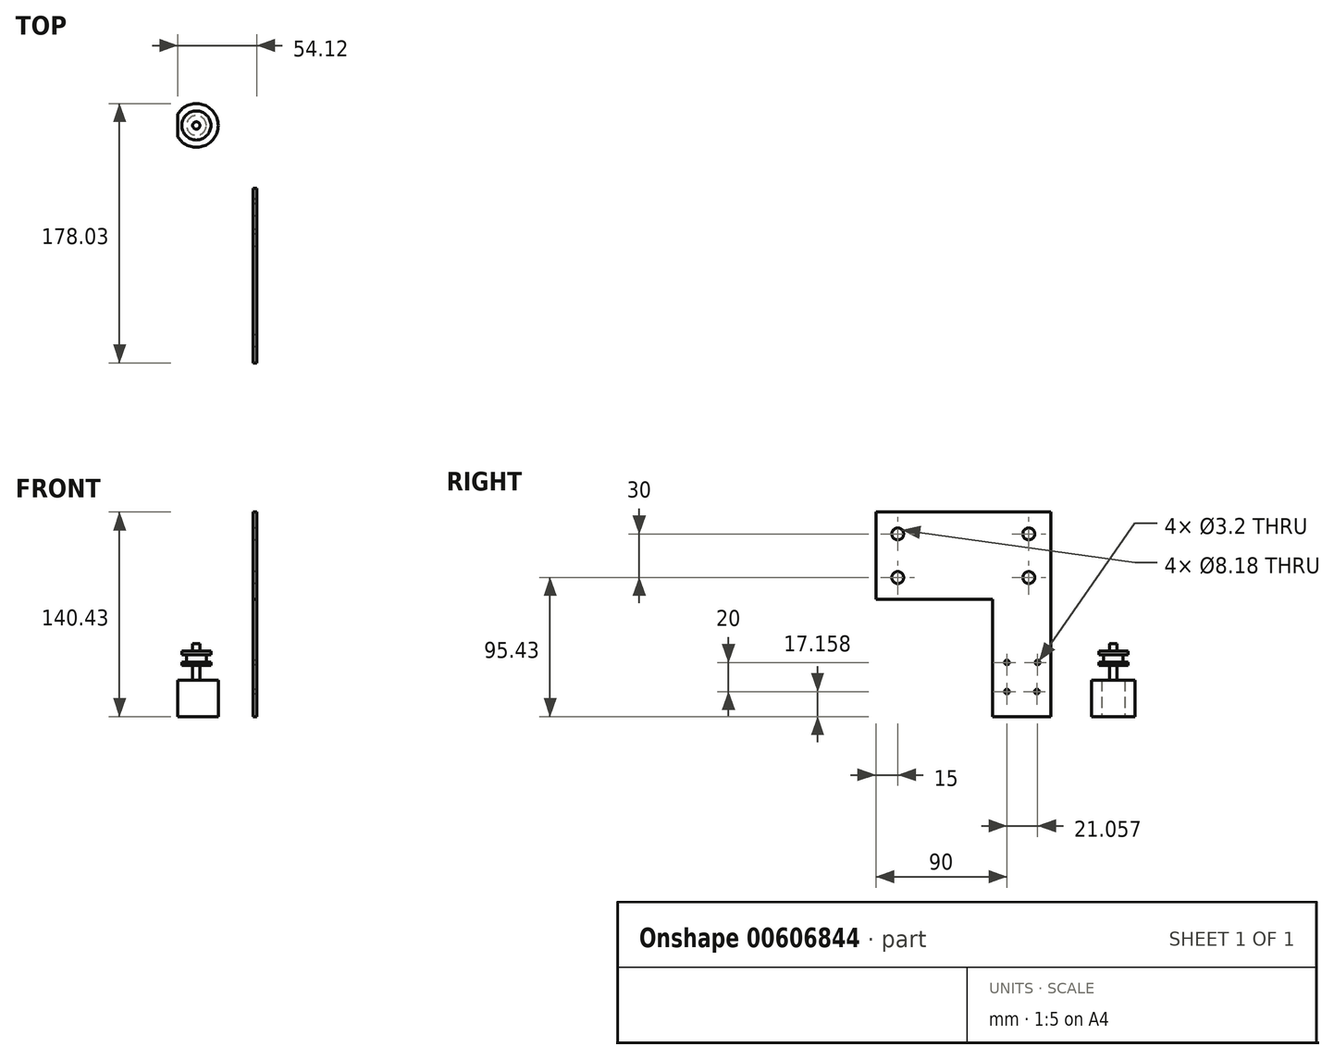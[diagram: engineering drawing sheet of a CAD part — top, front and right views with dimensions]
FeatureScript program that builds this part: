
annotation { "Feature Type Name" : "Feature", "Feature Type Description" : "" }
export const myFeature = defineFeature(function(context is Context, id is Id, definition is map)
    precondition{}
    {
        {
            var Q0;
            Q0=qCreatedBy(makeId("Right.planeOp"),FACE);
            var sketch = newSketch(context, id + "F0", { "sketchPlane" : qUnion([Q0])});
            skLineSegment(sketch, "E0", {"start": v(0, 0) * mm, "end": v(0, 140.43) * mm});
            skLineSegment(sketch, "E1", {"start": v(0, 140.43) * mm, "end": v(-120, 140.43) * mm});
            skLineSegment(sketch, "E2", {"start": v(-120, 140.43) * mm, "end": v(-120, 80.43) * mm});
            skLineSegment(sketch, "E3", {"start": v(-120, 80.43) * mm, "end": v(-40, 80.43) * mm});
            skLineSegment(sketch, "E4", {"start": v(-40, 80.43) * mm, "end": v(-40, 0) * mm});
            skLineSegment(sketch, "E5", {"start": v(-40, 0) * mm, "end": v(0, 0) * mm});
            skLineSegment(sketch, "E6", {"start": v(-40, 60) * mm, "end": v(0, 60) * mm, "construction": true});
            skLineSegment(sketch, "E7", {"start": v(-40, 30) * mm, "end": v(0, 30) * mm, "construction": true});
            skCircle(sketch, "E8.MirrorC", {"center": v(-9.46, 17.16) * mm, "radius": 1.6 * mm});
            skCircle(sketch, "E9", {"center": v(-8.94, 37.16) * mm, "radius": 1.6 * mm});
            skCircle(sketch, "E10.MirrorC", {"center": v(-30, 37.16) * mm, "radius": 1.6 * mm});
            skCircle(sketch, "E11.MirrorC", {"center": v(-30, 17.16) * mm, "radius": 1.6 * mm});
            skPoint(sketch, "E12.endSnap0", {"position": v(-60, 110.43) * mm});
            skCircle(sketch, "E13", {"center": v(-15, 125.43) * mm, "radius": 4.1 * mm});
            skCircle(sketch, "E14.MirrorC", {"center": v(-105, 125.43) * mm, "radius": 4.1 * mm});
            skCircle(sketch, "E15.MirrorC", {"center": v(-105, 95.43) * mm, "radius": 4.1 * mm});
            skCircle(sketch, "E16.MirrorC", {"center": v(-15, 95.43) * mm, "radius": 4.1 * mm});
            skCircle(sketch, "E17", {"center": v(-60, 110.43) * mm, "radius": 8.52 * mm});
            skSolve(sketch);
        }
        {
            var Q0;
            {var subQ1=sQuery(id+"F0.wireOp",EDGE,"E0");Q0=makeQuery(id+"F0.imprint","IMPRINT",FACE,{"disambiguationData":[TD([[makeQuery(id+"F0.imprint","IMPRINT",EDGE,{"derivedFrom":subQ1}),1.0]])]});}
            var Q1;
            Q1=makeQuery(id+"F0.imprint","IMPRINT",FACE,{"disambiguationData":[TD([[makeQuery(id+"F0.imprint","IMPRINT",EDGE,{"derivedFrom":sQuery(id+"F0.wireOp",EDGE,"E17")}),1.0]])]});
            extrude(context, id + "F1", {"entities" : qUnion([Q0, Q1]), "depth" : 2.5 * mm, "offsetDistance" : 25 * mm});
        }
        {
            var Q0;
            Q0=qCreatedBy(makeId("Top.planeOp"),FACE);
            var sketch = newSketch(context, id + "F2", { "sketchPlane" : qUnion([Q0])});
            skCircle(sketch, "E18", {"center": v(-38.93, 43.03) * mm, "radius": 15 * mm});
            skLineSegment(sketch, "E19", {"start": v(-51.62, 43.03) * mm, "end": v(-51.62, 35.03) * mm});
            skLineSegment(sketch, "E20.MirrorCS", {"start": v(-51.62, 43.03) * mm, "end": v(-51.62, 51.03) * mm});
            skSolve(sketch);
        }
        {
            var Q0;
            {var subQ0=sQuery(id+"F2.wireOp",EDGE,"E19");Q0=makeQuery(id+"F2.imprint","IMPRINT",FACE,{"disambiguationData":[TD([[makeQuery(id+"F2.imprint","IMPRINT",EDGE,{"derivedFrom":subQ0}),1.0]])]});}
            extrude(context, id + "F3", {"entities" : qUnion([Q0]), "depth" : 25 * mm, "offsetDistance" : 25 * mm});
        }
        {
            var Q0;
            Q0=makeQuery(id+"F3.opExtrude","CAP_FACE",FACE,{"disambiguationData":[OSD([sQuery(id+"F2.wireOp",EDGE,"E18"),sQuery(id+"F2.wireOp",EDGE,"E19"),sQuery(id+"F2.wireOp",EDGE,"E20.MirrorCS")])],"isStart":false});
            var sketch = newSketch(context, id + "F4", { "sketchPlane" : qUnion([Q0])});
            skCircle(sketch, "E21", {"center": v(-38.93, 43.03) * mm, "radius": 2.5 * mm});
            skSolve(sketch);
        }
        {
            var Q0;
            Q0=makeQuery(id+"F4.imprint","IMPRINT",FACE,{"disambiguationData":[TD([[makeQuery(id+"F4.imprint","IMPRINT",EDGE,{"derivedFrom":sQuery(id+"F4.wireOp",EDGE,"E21")}),1.0]])]});
            extrude(context, id + "F5", {"entities" : qUnion([Q0]), "operationType" : NewBodyOperationType.ADD, "depth" : 10 * mm, "offsetDistance" : 25 * mm});
        }
        {
            var Q0;
            Q0=makeQuery(id+"F5.opExtrude","CAP_FACE",FACE,{"disambiguationData":[OSD([sQuery(id+"F4.wireOp",EDGE,"E21")])],"isStart":false});
            var sketch = newSketch(context, id + "F6", { "sketchPlane" : qUnion([Q0])});
            skCircle(sketch, "E22", {"center": v(-38.93, 43.03) * mm, "radius": 10 * mm});
            skSolve(sketch);
        }
        {
            var Q0;
            Q0=makeQuery(id+"F6.imprint","IMPRINT",FACE,{"disambiguationData":[TD([[makeQuery(id+"F6.imprint","IMPRINT",EDGE,{"derivedFrom":sQuery(id+"F6.wireOp",EDGE,"E22")}),1.0]])]});
            var Q1;
            Q1=makeQuery(id+"F6.imprint","IMPRINT",FACE,{"disambiguationData":[TD([[makeQuery(id+"F6.imprint","IMPRINT",EDGE,{"derivedFrom":makeQuery(id+"F5.opExtrude","CAP_EDGE",EDGE,{"disambiguationData":[OSD([sQuery(id+"F4.wireOp",EDGE,"E21")])],"isStart":false})}),1.0]])]});
            extrude(context, id + "F7", {"entities" : qUnion([Q0, Q1]), "operationType" : NewBodyOperationType.ADD, "depth" : 2.5 * mm, "offsetDistance" : 25 * mm});
        }
        {
            var Q0;
            Q0=makeQuery(id+"F7.opExtrude","CAP_FACE",FACE,{"disambiguationData":[OSD([sQuery(id+"F6.wireOp",EDGE,"E22")])],"isStart":false});
            var sketch = newSketch(context, id + "F8", { "sketchPlane" : qUnion([Q0])});
            skCircle(sketch, "E23", {"center": v(-38.93, 43.03) * mm, "radius": 6.78 * mm});
            skSolve(sketch);
        }
        {
            var Q0;
            Q0=makeQuery(id+"F8.imprint","IMPRINT",FACE,{"disambiguationData":[TD([[makeQuery(id+"F8.imprint","IMPRINT",EDGE,{"derivedFrom":sQuery(id+"F8.wireOp",EDGE,"E23")}),1.0]])]});
            extrude(context, id + "F9", {"entities" : qUnion([Q0]), "operationType" : NewBodyOperationType.ADD, "depth" : 5 * mm, "offsetDistance" : 25 * mm});
        }
        {
            var Q0;
            Q0=makeQuery(id+"F9.opExtrude","CAP_FACE",FACE,{"disambiguationData":[OSD([sQuery(id+"F8.wireOp",EDGE,"E23")])],"isStart":false});
            var sketch = newSketch(context, id + "F10", { "sketchPlane" : qUnion([Q0])});
            skCircle(sketch, "E24", {"center": v(-38.93, 43.03) * mm, "radius": 10 * mm});
            skSolve(sketch);
        }
        {
            var Q0;
            Q0=makeQuery(id+"F10.imprint","IMPRINT",FACE,{"disambiguationData":[TD([[makeQuery(id+"F10.imprint","IMPRINT",EDGE,{"derivedFrom":sQuery(id+"F10.wireOp",EDGE,"E24")}),1.0]])]});
            var Q1;
            Q1=makeQuery(id+"F10.imprint","IMPRINT",FACE,{"disambiguationData":[TD([[makeQuery(id+"F10.imprint","IMPRINT",EDGE,{"derivedFrom":makeQuery(id+"F9.opExtrude","CAP_EDGE",EDGE,{"disambiguationData":[OSD([sQuery(id+"F8.wireOp",EDGE,"E23")])],"isStart":false})}),1.0]])]});
            extrude(context, id + "F11", {"entities" : qUnion([Q0, Q1]), "operationType" : NewBodyOperationType.ADD, "depth" : 2.5 * mm, "offsetDistance" : 25 * mm});
        }
        {
            var Q0;
            Q0=makeQuery(id+"F11.opExtrude","CAP_FACE",FACE,{"disambiguationData":[OSD([sQuery(id+"F10.wireOp",EDGE,"E24")])],"isStart":false});
            var sketch = newSketch(context, id + "F12", { "sketchPlane" : qUnion([Q0])});
            skCircle(sketch, "E25", {"center": v(-38.93, 43.03) * mm, "radius": 2.5 * mm});
            skSolve(sketch);
        }
        {
            var Q0;
            Q0=makeQuery(id+"F12.imprint","IMPRINT",FACE,{"disambiguationData":[TD([[makeQuery(id+"F12.imprint","IMPRINT",EDGE,{"derivedFrom":sQuery(id+"F12.wireOp",EDGE,"E25")}),1.0]])]});
            extrude(context, id + "F13", {"entities" : qUnion([Q0]), "operationType" : NewBodyOperationType.ADD, "depth" : 5 * mm, "offsetDistance" : 25 * mm});
        }
    });
